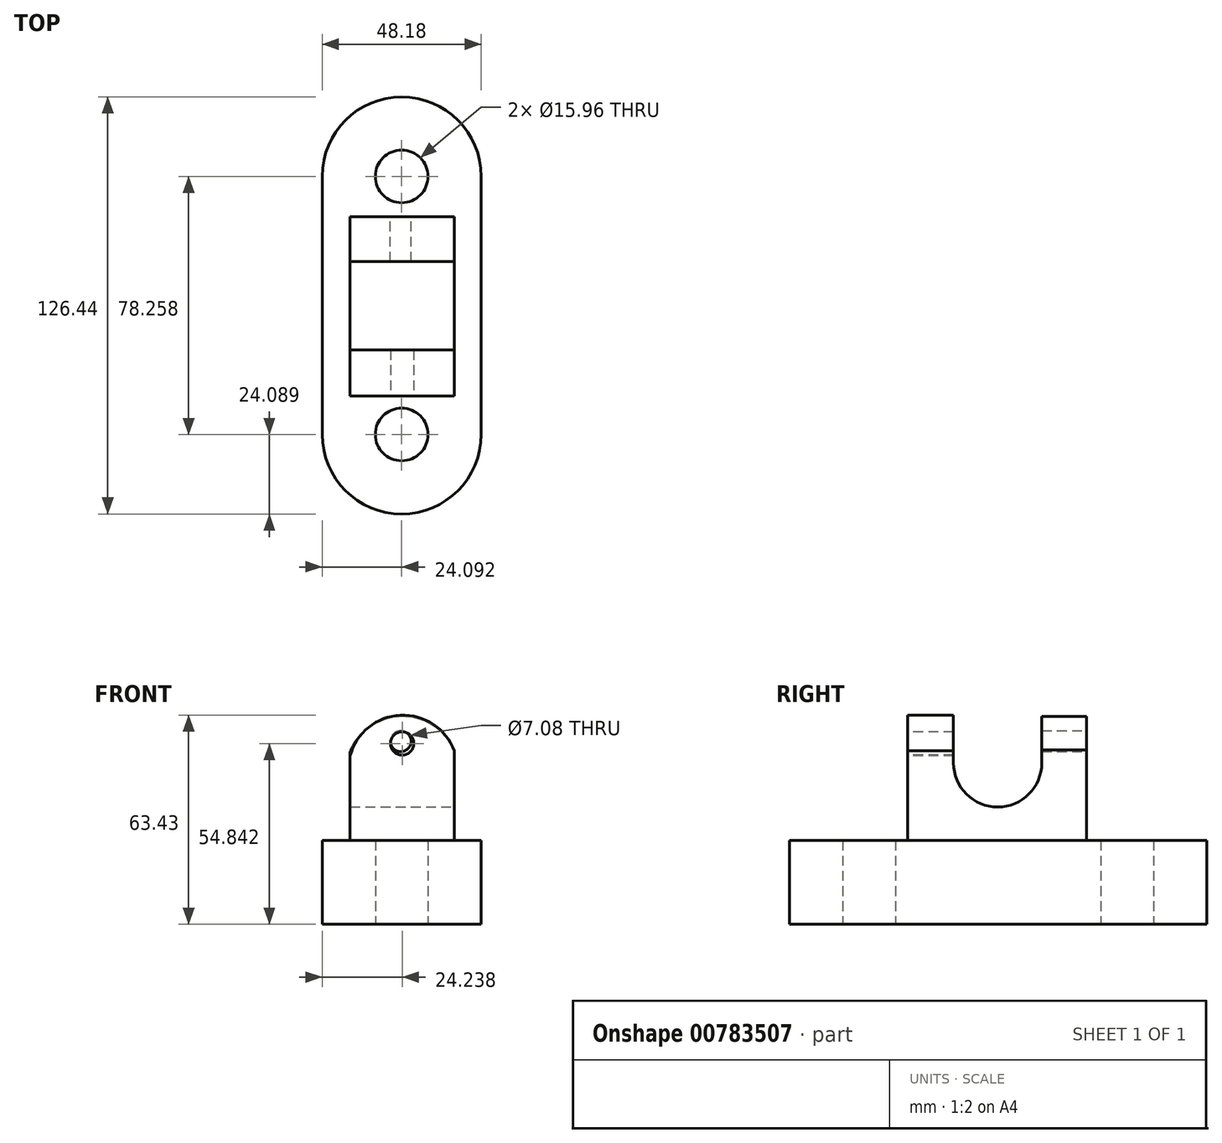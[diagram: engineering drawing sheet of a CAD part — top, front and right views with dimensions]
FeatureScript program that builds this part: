
annotation { "Feature Type Name" : "Feature", "Feature Type Description" : "" }
export const myFeature = defineFeature(function(context is Context, id is Id, definition is map)
    precondition{}
    {
        {
            var Q0;
            Q0=qCreatedBy(makeId("Top.planeOp"),FACE);
            var sketch = newSketch(context, id + "F0", { "sketchPlane" : qUnion([Q0])});
            skLineSegment(sketch, "E0", {"start": v(-23.8, 0) * mm, "end": v(24.38, 0) * mm, "construction": true});
            skArc(sketch, "E1", {"start": v(24.38, 39.57) * mm, "mid": v(0.3, 63.66) * mm, "end": v(-23.8, 39.57) * mm});
            skArc(sketch, "E2", {"start": v(-23.8, -38.7) * mm, "mid": v(0.3, -62.78) * mm, "end": v(24.38, -38.7) * mm});
            skLineSegment(sketch, "E3", {"start": v(-23.8, 39.57) * mm, "end": v(-23.8, -38.7) * mm});
            skLineSegment(sketch, "E4", {"start": v(24.38, -38.7) * mm, "end": v(24.38, 39.57) * mm});
            skCircle(sketch, "E5", {"center": v(0.3, 39.57) * mm, "radius": 7.98 * mm});
            skCircle(sketch, "E6", {"center": v(0.3, -38.7) * mm, "radius": 7.98 * mm});
            skSolve(sketch);
        }
        {
            var Q0;
            Q0=makeQuery(id+"F0.imprint","IMPRINT",FACE,{"disambiguationData":[TD([[makeQuery(id+"F0.imprint","IMPRINT",EDGE,{"derivedFrom":sQuery(id+"F0.wireOp",EDGE,"E1")}),1.0]])]});
            extrude(context, id + "F1", {"entities" : qUnion([Q0]), "depth" : 25.4 * mm, "offsetDistance" : 25.4 * mm});
        }
        {
            var Q0;
            Q0=makeQuery(id+"F1.opExtrude","CAP_FACE",FACE,{"disambiguationData":[OSD([sQuery(id+"F0.wireOp",EDGE,"E1"),sQuery(id+"F0.wireOp",EDGE,"E2"),sQuery(id+"F0.wireOp",EDGE,"E3"),sQuery(id+"F0.wireOp",EDGE,"E4"),sQuery(id+"F0.wireOp",EDGE,"E5"),sQuery(id+"F0.wireOp",EDGE,"E6")])],"isStart":false});
            var sketch = newSketch(context, id + "F2", { "sketchPlane" : qUnion([Q0])});
            skLineSegment(sketch, "E7.bottom", {"start": v(-15.33, 27.3) * mm, "end": v(16.2, 27.3) * mm});
            skLineSegment(sketch, "E7.top", {"start": v(-15.33, -27.01) * mm, "end": v(16.2, -27.01) * mm});
            skLineSegment(sketch, "E7.left", {"start": v(-15.33, 27.3) * mm, "end": v(-15.33, -27.01) * mm});
            skLineSegment(sketch, "E7.right", {"start": v(16.2, 27.3) * mm, "end": v(16.2, -27.01) * mm});
            skSolve(sketch);
        }
        {
            var Q0;
            Q0=makeQuery(id+"F2.imprint","IMPRINT",FACE,{"disambiguationData":[TD([[makeQuery(id+"F2.imprint","IMPRINT",EDGE,{"derivedFrom":sQuery(id+"F2.wireOp",EDGE,"E7.bottom")}),-1.0]])]});
            extrude(context, id + "F3", {"entities" : qUnion([Q0]), "operationType" : NewBodyOperationType.ADD, "depth" : 38.1 * mm, "offsetDistance" : 25.4 * mm});
        }
        {
            var Q0;
            Q0=makeQuery(id+"F3.opExtrude","SWEPT_FACE",FACE,{"disambiguationData":[OSD([sQuery(id+"F2.wireOp",EDGE,"E7.right")])]});
            var sketch = newSketch(context, id + "F4", { "sketchPlane" : qUnion([Q0])});
            skLineSegment(sketch, "E8", {"start": v(13.7, 63.5) * mm, "end": v(13.7, 48.94) * mm});
            skArc(sketch, "E9", {"start": v(-13.07, 48.94) * mm, "mid": v(0.31, 35.56) * mm, "end": v(13.7, 48.94) * mm});
            skLineSegment(sketch, "E10", {"start": v(-13.07, 48.94) * mm, "end": v(-13.07, 63.5) * mm});
            skSolve(sketch);
        }
        {
            var Q0;
            {var subQ0=sQuery(id+"F4.wireOp",EDGE,"E8");Q0=makeQuery(id+"F4.imprint","IMPRINT",FACE,{"disambiguationData":[TD([[makeQuery(id+"F4.imprint","IMPRINT",EDGE,{"derivedFrom":subQ0}),-1.0]])]});}
            extrude(context, id + "F5", {"entities" : qUnion([Q0]), "operationType" : NewBodyOperationType.REMOVE, "oppositeDirection" : true, "depth" : 35.56 * mm, "offsetDistance" : 25.4 * mm});
        }
        {
            var Q0;
            Q0=makeQuery(id+"F3.opExtrude","SWEPT_FACE",FACE,{"disambiguationData":[OSD([sQuery(id+"F2.wireOp",EDGE,"E7.top")])]});
            var sketch = newSketch(context, id + "F6", { "sketchPlane" : qUnion([Q0])});
            skArc(sketch, "E11", {"start": v(16.2, 52.57) * mm, "mid": v(-0.1, 63.42) * mm, "end": v(-15.33, 51.12) * mm});
            skSolve(sketch);
        }
        {
            var Q0;
            {var subQ0=sQuery(id+"F6.wireOp",EDGE,"E11");Q0=makeQuery(id+"F6.imprint","IMPRINT",FACE,{"disambiguationData":[TD([[makeQuery(id+"F6.imprint","IMPRINT",EDGE,{"derivedFrom":subQ0}),-1.0]])]});}
            extrude(context, id + "F7", {"entities" : qUnion([Q0]), "operationType" : NewBodyOperationType.REMOVE, "oppositeDirection" : true, "depth" : 33.02 * mm, "offsetDistance" : 25.4 * mm});
        }
        {
            var Q0;
            Q0=makeQuery(id+"F3.opExtrude","SWEPT_FACE",FACE,{"disambiguationData":[OSD([sQuery(id+"F2.wireOp",EDGE,"E7.bottom")])]});
            var sketch = newSketch(context, id + "F8", { "sketchPlane" : qUnion([Q0])});
            skArc(sketch, "E12", {"start": v(15.33, 52.32) * mm, "mid": v(-0.27, 63) * mm, "end": v(-16.2, 52.83) * mm});
            skSolve(sketch);
        }
        {
            var Q0;
            {var subQ0=sQuery(id+"F8.wireOp",EDGE,"E12");Q0=makeQuery(id+"F8.imprint","IMPRINT",FACE,{"disambiguationData":[TD([[makeQuery(id+"F8.imprint","IMPRINT",EDGE,{"derivedFrom":subQ0}),-1.0]])]});}
            extrude(context, id + "F9", {"entities" : qUnion([Q0]), "operationType" : NewBodyOperationType.REMOVE, "oppositeDirection" : true, "depth" : 33.02 * mm, "offsetDistance" : 25.4 * mm});
        }
        {
            var Q0;
            Q0=makeQuery(id+"F3.opExtrude","SWEPT_FACE",FACE,{"disambiguationData":[OSD([sQuery(id+"F2.wireOp",EDGE,"E7.bottom")])]});
            var sketch = newSketch(context, id + "F10", { "sketchPlane" : qUnion([Q0])});
            skCircle(sketch, "E13", {"center": v(0, 55.53) * mm, "radius": 3.16 * mm});
            skSolve(sketch);
        }
        {
            var Q0;
            Q0=makeQuery(id+"F10.imprint","IMPRINT",FACE,{"disambiguationData":[TD([[makeQuery(id+"F10.imprint","IMPRINT",EDGE,{"derivedFrom":sQuery(id+"F10.wireOp",EDGE,"E13")}),1.0]])]});
            extrude(context, id + "F11", {"entities" : qUnion([Q0]), "operationType" : NewBodyOperationType.REMOVE, "oppositeDirection" : true, "depth" : 33.02 * mm, "offsetDistance" : 25.4 * mm});
        }
        {
            var Q0;
            Q0=makeQuery(id+"F3.opExtrude","SWEPT_FACE",FACE,{"disambiguationData":[OSD([sQuery(id+"F2.wireOp",EDGE,"E7.top")])]});
            var sketch = newSketch(context, id + "F12", { "sketchPlane" : qUnion([Q0])});
            skCircle(sketch, "E14", {"center": v(0.44, 54.84) * mm, "radius": 3.54 * mm});
            skPoint(sketch, "E14.centerSnap0", {"position": v(0.44, 25.4) * mm});
            skSolve(sketch);
        }
        {
            var Q0;
            Q0=makeQuery(id+"F12.imprint","IMPRINT",FACE,{"disambiguationData":[TD([[makeQuery(id+"F12.imprint","IMPRINT",EDGE,{"derivedFrom":sQuery(id+"F12.wireOp",EDGE,"E14")}),1.0]])]});
            extrude(context, id + "F13", {"entities" : qUnion([Q0]), "operationType" : NewBodyOperationType.REMOVE, "oppositeDirection" : true, "depth" : 33.02 * mm, "offsetDistance" : 25.4 * mm});
        }
    });
